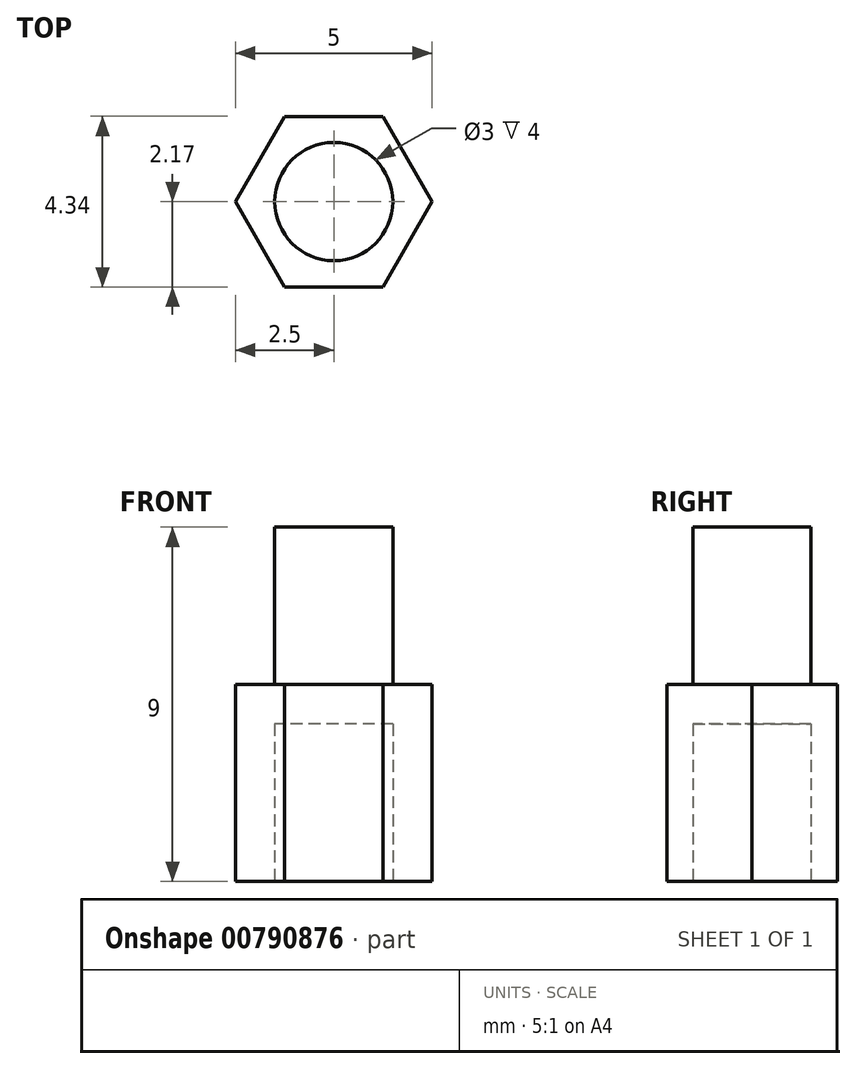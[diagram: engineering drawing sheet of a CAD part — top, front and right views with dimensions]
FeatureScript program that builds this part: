
annotation { "Feature Type Name" : "Feature", "Feature Type Description" : "" }
export const myFeature = defineFeature(function(context is Context, id is Id, definition is map)
    precondition{}
    {
        {
            var Q0;
            Q0=qCreatedBy(makeId("Top.planeOp"),FACE);
            var sketch = newSketch(context, id + "F0", { "sketchPlane" : qUnion([Q0])});
            skCircle(sketch, "E0.cCircle", {"center": v(0, 0) * mm, "radius": 2.5 * mm, "construction": true});
            skLineSegment(sketch, "E0.0", {"start": v(2.5, 0) * mm, "end": v(1.25, -2.17) * mm});
            skLineSegment(sketch, "E0.1", {"start": v(1.25, -2.17) * mm, "end": v(-1.25, -2.17) * mm});
            skLineSegment(sketch, "E0.2", {"start": v(-1.25, -2.17) * mm, "end": v(-2.5, 0) * mm});
            skLineSegment(sketch, "E0.3", {"start": v(-2.5, 0) * mm, "end": v(-1.25, 2.17) * mm});
            skLineSegment(sketch, "E0.4", {"start": v(-1.25, 2.17) * mm, "end": v(1.25, 2.17) * mm});
            skLineSegment(sketch, "E0.5", {"start": v(1.25, 2.17) * mm, "end": v(2.5, 0) * mm});
            skSolve(sketch);
        }
        {
            var Q0;
            Q0=makeQuery(id+"F0.imprint","IMPRINT",FACE,{"disambiguationData":[TD([[makeQuery(id+"F0.imprint","IMPRINT",EDGE,{"derivedFrom":sQuery(id+"F0.wireOp",EDGE,"E0.0")}),-1.0]])]});
            extrude(context, id + "F1", {"entities" : qUnion([Q0]), "depth" : 5 * mm, "offsetDistance" : 25 * mm});
        }
        {
            var Q0;
            Q0=makeQuery(id+"F1.opExtrude","CAP_FACE",FACE,{"disambiguationData":[OSD([sQuery(id+"F0.wireOp",EDGE,"E0.0"),sQuery(id+"F0.wireOp",EDGE,"E0.1"),sQuery(id+"F0.wireOp",EDGE,"E0.2"),sQuery(id+"F0.wireOp",EDGE,"E0.3"),sQuery(id+"F0.wireOp",EDGE,"E0.4"),sQuery(id+"F0.wireOp",EDGE,"E0.5")])],"isStart":false});
            var sketch = newSketch(context, id + "F2", { "sketchPlane" : qUnion([Q0])});
            skCircle(sketch, "E1", {"center": v(0, 0) * mm, "radius": 1.5 * mm});
            skSolve(sketch);
        }
        {
            var Q0;
            Q0=makeQuery(id+"F2.imprint","IMPRINT",FACE,{"disambiguationData":[TD([[makeQuery(id+"F2.imprint","IMPRINT",EDGE,{"derivedFrom":sQuery(id+"F2.wireOp",EDGE,"E1")}),1.0]])]});
            extrude(context, id + "F3", {"entities" : qUnion([Q0]), "operationType" : NewBodyOperationType.ADD, "depth" : 4 * mm, "offsetDistance" : 25 * mm});
        }
        {
            var Q0;
            Q0=makeQuery(id+"F0.imprint","IMPRINT",FACE,{"disambiguationData":[TD([[makeQuery(id+"F0.imprint","IMPRINT",EDGE,{"derivedFrom":sQuery(id+"F0.wireOp",EDGE,"E0.0")}),-1.0]])]});
            var sketch = newSketch(context, id + "F4", { "sketchPlane" : qUnion([Q0])});
            skCircle(sketch, "E2", {"center": v(0, 0) * mm, "radius": 1.5 * mm});
            skSolve(sketch);
        }
        {
            var Q0;
            Q0 = qSketchRegion(id + "F4", true);
            extrude(context, id + "F5", {"entities" : qUnion([Q0]), "operationType" : NewBodyOperationType.REMOVE, "depth" : 4 * mm, "offsetDistance" : 25 * mm});
        }
    });
